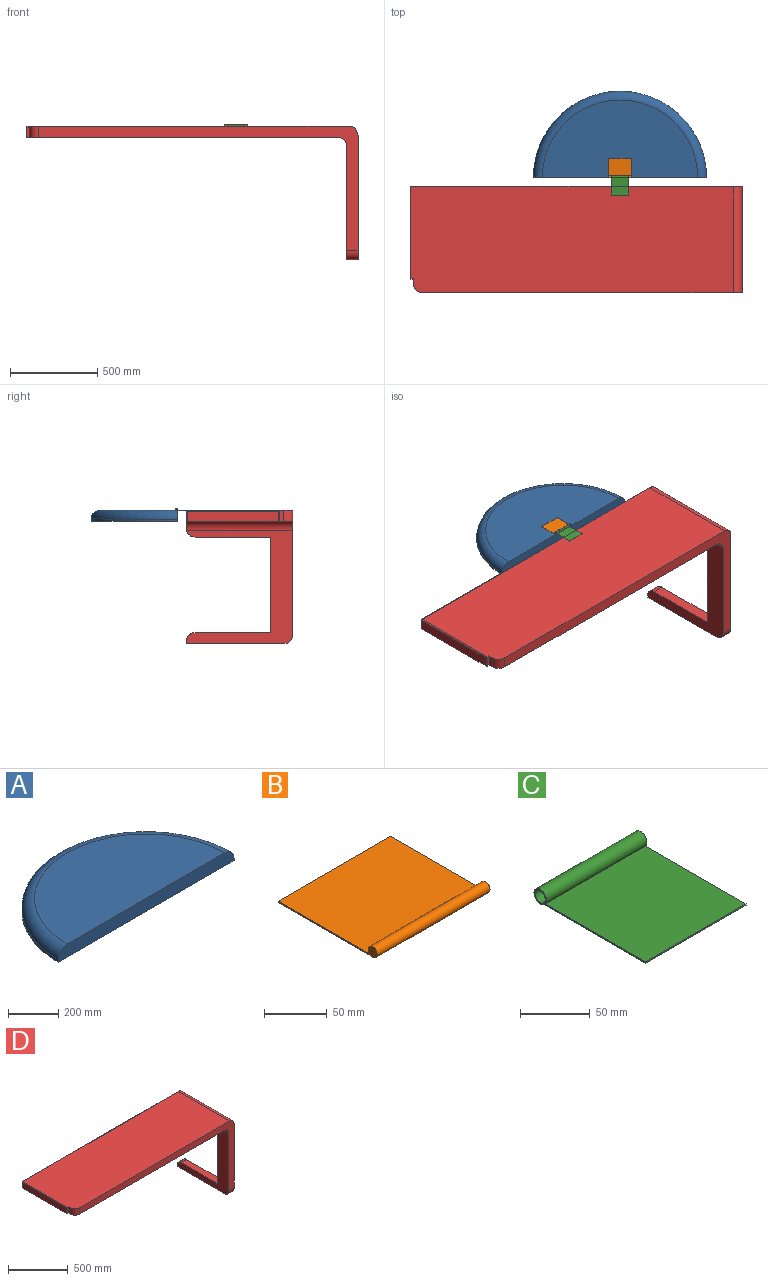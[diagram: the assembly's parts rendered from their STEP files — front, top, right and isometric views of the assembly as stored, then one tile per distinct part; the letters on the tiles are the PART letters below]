
ASSEMBLY  parts=4 mates=3
PART A: 5 faces, bbox 1072.2x536.1x63.5 mm
  f0: plane 990.6x63.5mm, normal (0,-1,0), area 61795.5mm2, adj f1,f2,f3,f4
  f1: cylinder r=495.3mm len=990.6mm, axis (0,0,1), area 19761.6mm2, adj f0,f2,f4
  f2: plane 990.6x495.3mm, normal (0,0,-1), area 385351mm2, adj f0,f1
  f3: plane 889x444.5mm, normal (0,0,1), area 310358.3mm2, adj f0,f4
  f4: torus R=444.5mm, axis (0,0,1), area 119538.1mm2, adj f0,f1,f3
PART B: 13 faces, bbox 127x111.8x10.2 mm
  f0: plane 12.7x0.96mm, normal (0,0.66,0.75), area 16.2mm2, adj f3,f5,f7,f9
  f1: plane 127x1.63mm, normal (0,-0.64,-0.77), area 139.4mm2, adj f5,f6,f7,f8,f9,f10,f11,f12
  f2: plane 127x1.27mm, normal (0,1,0), area 161.3mm2, adj f3,f6,f7,f8
  f3: plane 127x101.6mm, normal (0,0,1), area 12903.2mm2, adj f0,f2,f4,f7,f8,f12
  f4: plane 12.7x0.96mm, normal (0,0.66,0.75), area 16.2mm2, adj f3,f5,f8,f11
  f5: cylinder r=5.08mm len=127mm, axis (1,0,0), area 3924.7mm2, adj f0,f1,f4,f7,f8,f10
  f6: plane 127x101.6mm, normal (0,0,-1), area 12903.2mm2, adj f1,f2,f7,f8
  f7: plane 111.76x10.16mm, normal (-1,0,0), area 211.8mm2, adj f0,f1,f2,f3,f5,f6
  f8: plane 111.76x10.16mm, normal (1,0,0), area 211.8mm2, adj f1,f2,f3,f4,f5,f6
  f9: plane 1.63x1.58mm, normal (1,0,0), area 1.3mm2, adj f0,f1,f10,f12
  f10: plane 101.6x0.76mm, normal (0,0.75,-0.66), area 102.9mm2, adj f1,f5,f9,f11
  f11: plane 1.63x1.58mm, normal (-1,0,0), area 1.3mm2, adj f1,f4,f10,f12
  f12: plane 101.6x0.74mm, normal (0,-0.75,0.66), area 99.5mm2, adj f1,f3,f9,f11
PART C: 7 faces, bbox 101.6x113x12.7 mm
  f0: plane 101.6x101.6mm, normal (0,0,1), area 10322.6mm2, adj f1,f4,f5,f6
  f1: plane 101.6x1.27mm, normal (0,-1,0), area 129mm2, adj f0,f2,f5,f6
  f2: plane 102.87x101.6mm, normal (0,0,-1), area 10451.6mm2, adj f1,f4,f5,f6
  f3: cylinder r=5.08mm len=101.6mm, axis (1,0,0), area 3242.9mm2, adj f5,f6
  f4: cylinder r=6.35mm len=101.6mm, axis (1,0,0), area 3870.6mm2, adj f0,f2,f5,f6
  f5: plane 113.03x12.7mm, normal (-1,0,0), area 175.4mm2, adj f0,f1,f2,f3,f4
  f6: plane 113.03x12.7mm, normal (1,0,0), area 175.4mm2, adj f0,f1,f2,f3,f4
PART D: 33 faces, bbox 1902.8x613.8x766.2 mm
  f0: plane 647.7x609.6mm, normal (-1,0,0), area 129635.4mm2, adj f5,f6,f9,f10,f14,f15,f16,f17
  f1: plane 1888.49x96.52mm, normal (0,1,0), area 112649.8mm2, adj f4,f5,f18,f23,f26,f27,f28
  f2: plane 1842.77x604.52mm, normal (0,0,1), area 1112302mm2, adj f3,f8,f10,f13,f28,f30,f32
  f3: plane 63.5x30.48mm, normal (-1,0,0), area 1618.4mm2, adj f2,f4,f13,f20,f32
  f4: plane 1784.35x609.6mm, normal (0,0,-1), area 1085216.6mm2, adj f1,f3,f5,f10,f12,f13,f20,f21
  f5: cylinder r=50.8mm len=609.6mm, axis (0,-1,0), area 48637.1mm2, adj f0,f1,f4,f10,f18
  f6: plane 558.8x63.5mm, normal (0,0,-1), area 35483.8mm2, adj f0,f7,f9,f19
  f7: plane 711.2x609.6mm, normal (1,0,0), area 165501.5mm2, adj f6,f8,f9,f10,f14,f16,f17,f19
  f8: cylinder r=50.8mm len=604.52mm, axis (0,-1,0), area 48238.6mm2, adj f2,f7,f10,f27
  f9: plane 63.5x12.7mm, normal (0,1,0), area 806.5mm2, adj f0,f6,f7,f17
  f10: plane 1828.8x711.2mm, normal (0,-1,0), area 157257.8mm2, adj f0,f2,f4,f5,f7,f8,f13,f19
  f11: cone r=0mm half-angle=59deg, axis (0,0,-1), area 591.1mm2, adj f12
  f12: cylinder r=12.7mm len=25.4mm, axis (0,0,-1), area 1013.4mm2, adj f4,f11
  f13: cylinder r=50.8mm len=63.5mm, axis (0,0,-1), area 5067.1mm2, adj f2,f3,f4,f10
  f14: plane 551.18x63.5mm, normal (0,1,0), area 34682.9mm2, adj f0,f7,f15,f16,f24
  f15: plane 431.8x58.42mm, normal (0,0,-1), area 25225.8mm2, adj f0,f14,f18,f24
  f16: plane 431.8x63.5mm, normal (0,0,1), area 27419.3mm2, adj f0,f7,f14,f17
  f17: cylinder r=50.8mm len=63.5mm, axis (1,0,0), area 5067.1mm2, adj f0,f7,f9,f16
  f18: cylinder r=50.8mm len=60.03mm, axis (-1,0,0), area 4668.5mm2, adj f0,f1,f5,f15,f25
  f19: cylinder r=50.8mm len=63.5mm, axis (1,0,0), area 5067.1mm2, adj f0,f6,f7,f10
  f20: plane 58.42x13.97mm, normal (0,-1,0), area 816.1mm2, adj f3,f4,f22,f32
  f21: plane 523.24x58.42mm, normal (-1,0,0), area 30567.7mm2, adj f4,f22,f23,f30
  f22: cylinder r=5.08mm len=58.42mm, axis (0,0,-1), area 466.2mm2, adj f4,f20,f21,f31
  f23: cylinder r=5.08mm len=58.42mm, axis (0,0,1), area 466.2mm2, adj f1,f4,f21,f29
  f24: cylinder r=5.08mm len=431.8mm, axis (0,-1,0), area 3445.6mm2, adj f7,f14,f15,f25
  f25: torus R=45.72mm, axis (-1,0,0), area 613.6mm2, adj f7,f18,f24,f26
  f26: cylinder r=5.08mm len=50.8mm, axis (0,0,-1), area 405.4mm2, adj f1,f7,f25,f27
  f27: torus R=45.72mm, axis (0,-1,0), area 613.6mm2, adj f1,f8,f26,f28
  f28: cylinder r=5.08mm len=1842.77mm, axis (1,0,0), area 14704.7mm2, adj f1,f2,f27,f29
  f29: sphere r=5.08mm, area 40.5mm2, adj f23,f28,f30
  f30: cylinder r=5.08mm len=523.24mm, axis (0,1,0), area 4175.3mm2, adj f2,f21,f29,f31
  f31: sphere r=5.08mm, area 40.5mm2, adj f22,f30,f32
  f32: cylinder r=5.08mm len=13.97mm, axis (-1,0,0), area 111.5mm2, adj f2,f3,f20,f31
PLACE A rot(axis=(1,0,0),0.2deg) t=(1343.87,551.15,131.15)mm
PLACE B rot(axis=(1,0,0),0.2deg) t=(1407.37,557,109.04)mm
PLACE C t=(1394.67,457.79,153.1)mm
PLACE D t=(162.02,-105.81,131.17)mm
MATE revolute B.f5 <-> C.f3  axis (-1,0,0) through (1280.37,556.91,136.25)mm
MATE parallel C.f2 <-> D.f2  axis (0,0,-1) through (1343.87,501.66,131.17)mm
MATE parallel B.f6 <-> A.f3  axis (0,0,-1) through (1343.87,612.8,131.37)mm
